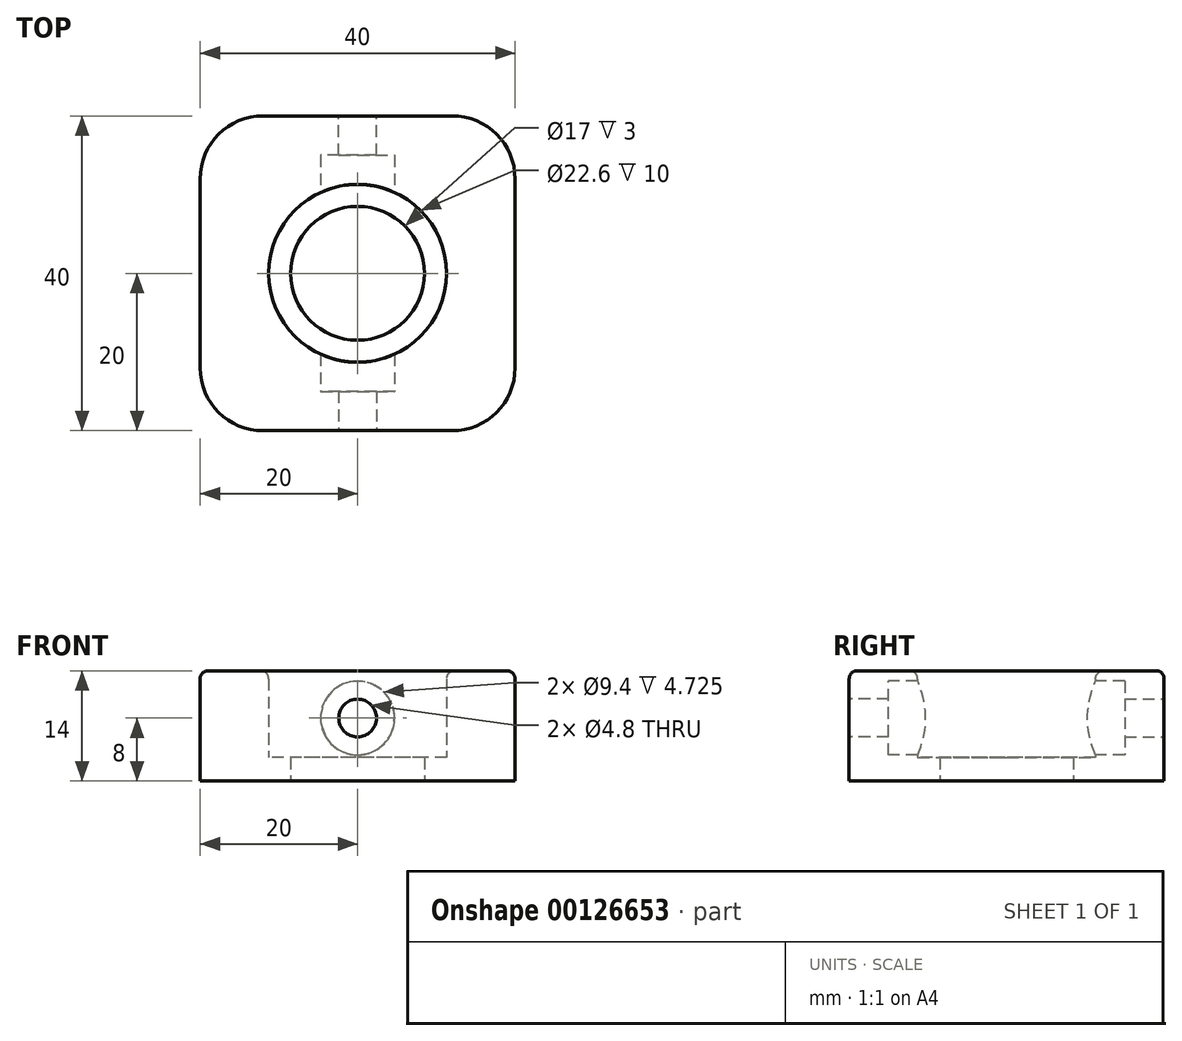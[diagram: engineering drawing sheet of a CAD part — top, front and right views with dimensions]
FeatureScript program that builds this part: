
annotation { "Feature Type Name" : "Feature", "Feature Type Description" : "" }
export const myFeature = defineFeature(function(context is Context, id is Id, definition is map)
    precondition{}
    {
        {
            var Q0;
            Q0=qCreatedBy(makeId("Top.planeOp"),FACE);
            var sketch = newSketch(context, id + "F0", { "sketchPlane" : qUnion([Q0])});
            skCircle(sketch, "E0", {"center": v(0, 0) * mm, "radius": 8.5 * mm});
            skCircle(sketch, "E1", {"center": v(0, 0) * mm, "radius": 11.3 * mm});
            skLineSegment(sketch, "E2.bottom", {"start": v(-20, 20) * mm, "end": v(20, 20) * mm});
            skLineSegment(sketch, "E2.top", {"start": v(-20, -20) * mm, "end": v(20, -20) * mm});
            skLineSegment(sketch, "E2.left", {"start": v(-20, 20) * mm, "end": v(-20, -20) * mm});
            skLineSegment(sketch, "E2.right", {"start": v(20, 20) * mm, "end": v(20, -20) * mm});
            skLineSegment(sketch, "E3", {"start": v(0, 20) * mm, "end": v(0, -20) * mm, "construction": true});
            skLineSegment(sketch, "E4", {"start": v(-20, 0) * mm, "end": v(20, 0) * mm, "construction": true});
            skSolve(sketch);
        }
        {
            var Q0;
            Q0=makeQuery(id+"F0.imprint","IMPRINT",FACE,{"disambiguationData":[TD([[makeQuery(id+"F0.imprint","IMPRINT",EDGE,{"derivedFrom":sQuery(id+"F0.wireOp",EDGE,"E0")}),-1.0]])]});
            extrude(context, id + "F1", {"entities" : qUnion([Q0]), "depth" : 3 * mm});
        }
        {
            var Q0;
            Q0=makeQuery(id+"F0.imprint","IMPRINT",FACE,{"disambiguationData":[TD([[makeQuery(id+"F0.imprint","IMPRINT",EDGE,{"derivedFrom":sQuery(id+"F0.wireOp",EDGE,"E1")}),-1.0]])]});
            extrude(context, id + "F2", {"entities" : qUnion([Q0]), "operationType" : NewBodyOperationType.ADD, "depth" : 14 * mm});
        }
        {
            var Q0;
            Q0=makeQuery(id+"F2.opExtrude","SWEPT_FACE",FACE,{"disambiguationData":[OSD([sQuery(id+"F0.wireOp",EDGE,"E2.top")])]});
            var sketch = newSketch(context, id + "F3", { "sketchPlane" : qUnion([Q0])});
            skCircle(sketch, "E5", {"center": v(0, 8) * mm, "radius": 4.7 * mm});
            skSolve(sketch);
        }
        {
            var Q0;
            Q0=makeQuery(id+"F3.imprint","IMPRINT",FACE,{"disambiguationData":[TD([[makeQuery(id+"F3.imprint","IMPRINT",EDGE,{"derivedFrom":sQuery(id+"F3.wireOp",EDGE,"E5")}),1.0]])]});
            extrude(context, id + "F4", {"entities" : qUnion([Q0]), "operationType" : NewBodyOperationType.REMOVE, "endBound" : BoundingType.THROUGH_ALL, "oppositeDirection" : true, "depth" : 25 * mm});
        }
        {
            var Q0;
            Q0=makeQuery(id+"F2.opExtrude","SWEPT_FACE",FACE,{"disambiguationData":[OSD([sQuery(id+"F0.wireOp",EDGE,"E2.top")])]});
            var sketch = newSketch(context, id + "F5", { "sketchPlane" : qUnion([Q0])});
            skCircle(sketch, "E6", {"center": v(0, 8) * mm, "radius": 2.4 * mm});
            skSolve(sketch);
        }
        {
            var Q0;
            Q0=makeQuery(id+"F5.imprint","IMPRINT",FACE,{"disambiguationData":[TD([[makeQuery(id+"F5.imprint","IMPRINT",EDGE,{"derivedFrom":sQuery(id+"F5.wireOp",EDGE,"E6")}),-1.0]])]});
            extrude(context, id + "F6", {"entities" : qUnion([Q0]), "operationType" : NewBodyOperationType.ADD, "oppositeDirection" : true, "depth" : 5 * mm});
        }
        {
            var Q0;
            Q0=makeQuery(id+"F2.opExtrude","SWEPT_FACE",FACE,{"disambiguationData":[OSD([sQuery(id+"F0.wireOp",EDGE,"E2.bottom")])]});
            var sketch = newSketch(context, id + "F7", { "sketchPlane" : qUnion([Q0])});
            skCircle(sketch, "E7", {"center": v(0, 8) * mm, "radius": 2.4 * mm});
            skSolve(sketch);
        }
        {
            var Q0;
            Q0=makeQuery(id+"F7.imprint","IMPRINT",FACE,{"disambiguationData":[TD([[makeQuery(id+"F7.imprint","IMPRINT",EDGE,{"derivedFrom":sQuery(id+"F7.wireOp",EDGE,"E7")}),-1.0]])]});
            extrude(context, id + "F8", {"entities" : qUnion([Q0]), "operationType" : NewBodyOperationType.ADD, "oppositeDirection" : true, "depth" : 5 * mm});
        }
        {
            var Q0;
            Q0=makeQuery(id+"F2.opExtrude","SWEPT_EDGE",EDGE,{"disambiguationData":[OSD([sQuery(id+"F0.wireOp",EDGE,"E2.top"),sQuery(id+"F0.wireOp",EDGE,"E2.left")])]});
            var Q1;
            Q1=makeQuery(id+"F2.opExtrude","SWEPT_EDGE",EDGE,{"disambiguationData":[OSD([sQuery(id+"F0.wireOp",EDGE,"E2.bottom"),sQuery(id+"F0.wireOp",EDGE,"E2.left")])]});
            var Q2;
            Q2=makeQuery(id+"F2.opExtrude","SWEPT_EDGE",EDGE,{"disambiguationData":[OSD([sQuery(id+"F0.wireOp",EDGE,"E2.top"),sQuery(id+"F0.wireOp",EDGE,"E2.right")])]});
            var Q3;
            Q3=makeQuery(id+"F2.opExtrude","SWEPT_EDGE",EDGE,{"disambiguationData":[OSD([sQuery(id+"F0.wireOp",EDGE,"E2.bottom"),sQuery(id+"F0.wireOp",EDGE,"E2.right")])]});
            fillet(context, id + "F9", {"entities" : qUnion([Q0, Q1, Q2, Q3]), "radius" : 8 * mm, "tangentPropagation" : true, "allowEdgeOverflow" : false});
        }
        {
            var Q0;
            Q0=makeQuery(id+"F2.opExtrude","CAP_EDGE",EDGE,{"disambiguationData":[OSD([sQuery(id+"F0.wireOp",EDGE,"E2.top")])],"isStart":false});
            var Q1;
            Q1=makeQuery(id+"F2.opExtrude","CAP_EDGE",EDGE,{"disambiguationData":[OSD([sQuery(id+"F0.wireOp",EDGE,"E1")])],"isStart":false});
            fillet(context, id + "F10", {"entities" : qUnion([Q0, Q1]), "radius" : 1 * mm, "tangentPropagation" : true, "allowEdgeOverflow" : false});
        }
    });
